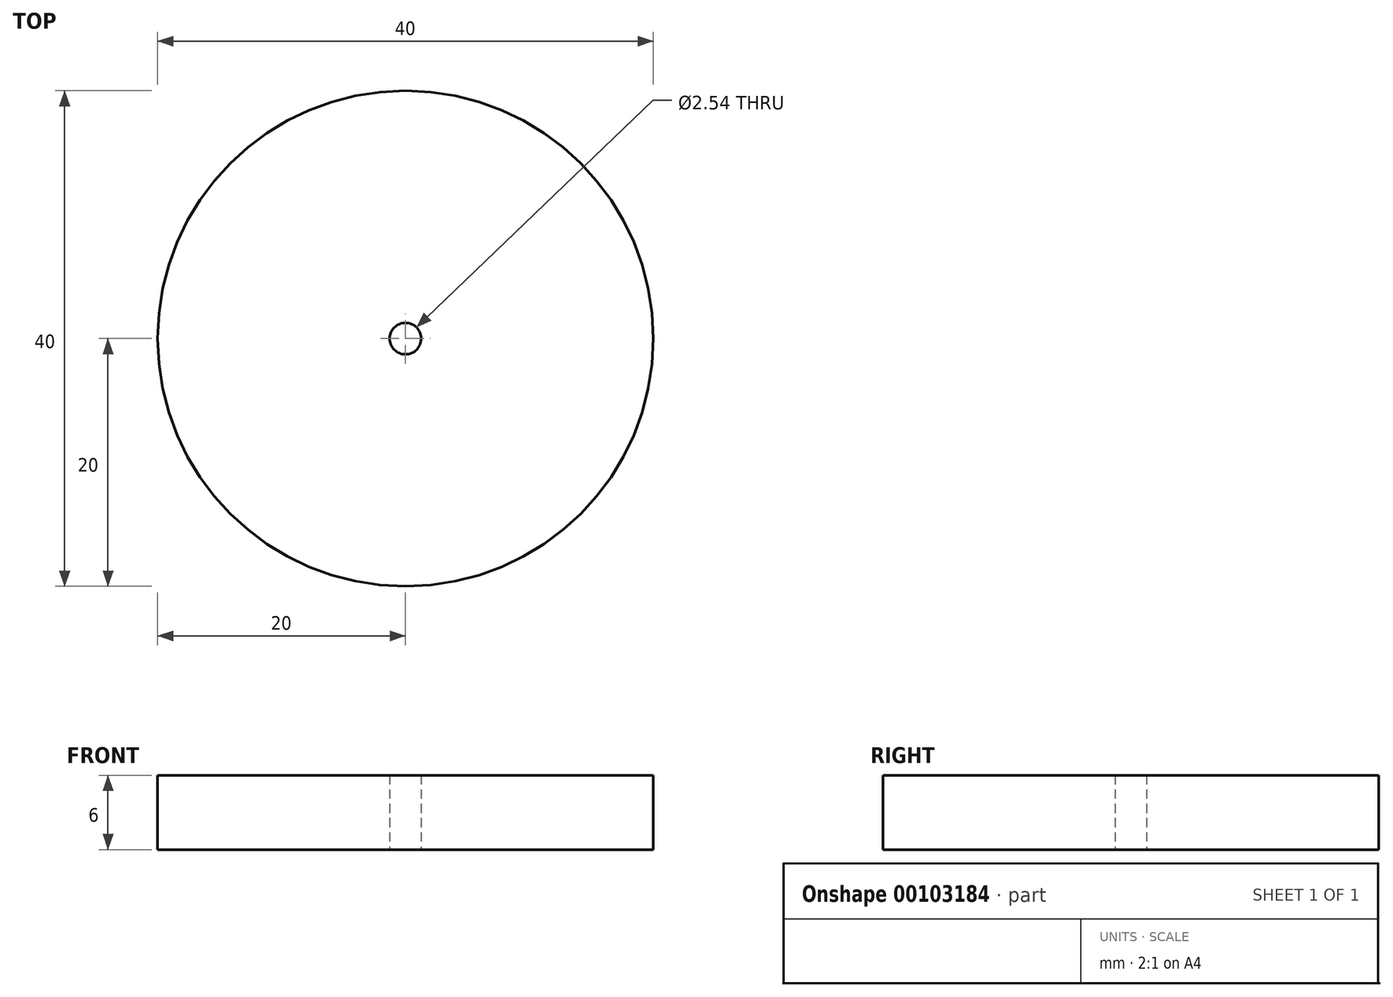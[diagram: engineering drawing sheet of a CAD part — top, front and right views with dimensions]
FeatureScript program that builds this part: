
annotation { "Feature Type Name" : "Feature", "Feature Type Description" : "" }
export const myFeature = defineFeature(function(context is Context, id is Id, definition is map)
    precondition{}
    {
        {
            var Q0;
            Q0=qCreatedBy(makeId("Top.planeOp"),FACE);
            var sketch = newSketch(context, id + "F0", { "sketchPlane" : qUnion([Q0])});
            skCircle(sketch, "E0", {"center": v(0, 0) * mm, "radius": 20 * mm});
            skCircle(sketch, "E1", {"center": v(0, 0) * mm, "radius": 1.27 * mm});
            skSolve(sketch);
        }
        {
            var Q0;
            Q0=makeQuery(id+"F0.imprint","IMPRINT",FACE,{"disambiguationData":[TD([[makeQuery(id+"F0.imprint","IMPRINT",EDGE,{"derivedFrom":sQuery(id+"F0.wireOp",EDGE,"E0")}),1.0]])]});
            extrude(context, id + "F1", {"entities" : qUnion([Q0]), "depth" : 6 * mm});
        }
    });
